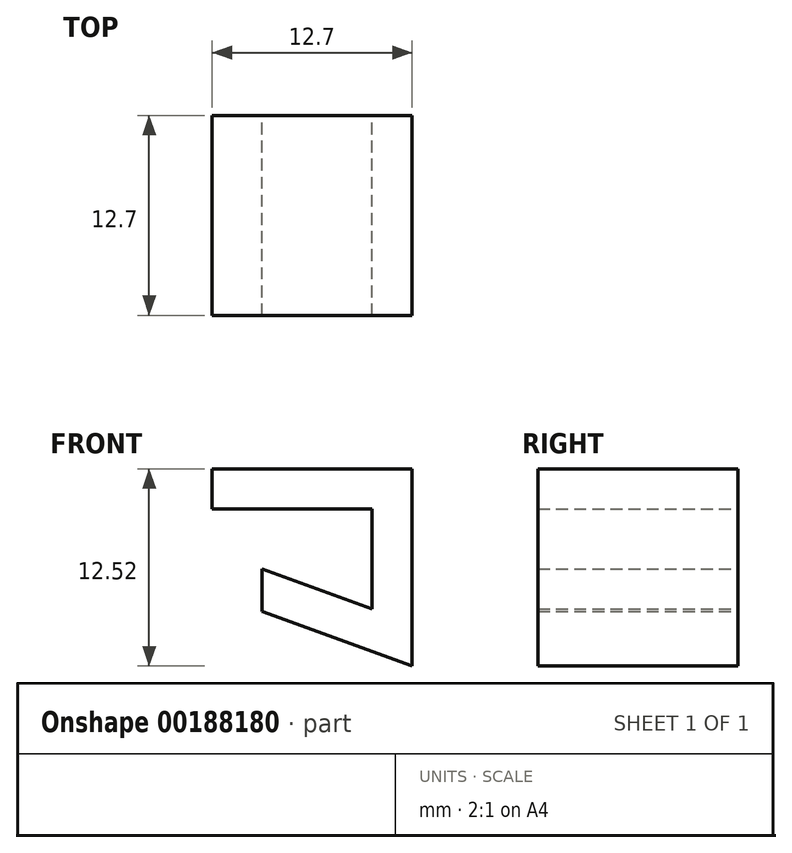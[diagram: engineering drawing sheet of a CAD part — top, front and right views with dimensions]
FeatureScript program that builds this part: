
annotation { "Feature Type Name" : "Feature", "Feature Type Description" : "" }
export const myFeature = defineFeature(function(context is Context, id is Id, definition is map)
    precondition{}
    {
        {
            var Q0;
            Q0=qCreatedBy(makeId("Front.planeOp"),FACE);
            var sketch = newSketch(context, id + "F0", { "sketchPlane" : qUnion([Q0])});
            skLineSegment(sketch, "E0", {"start": v(3.17, -6.35) * mm, "end": v(10.16, -8.89) * mm});
            skLineSegment(sketch, "E1", {"start": v(10.16, -8.89) * mm, "end": v(10.16, -2.54) * mm});
            skLineSegment(sketch, "E2", {"start": v(10.16, -2.54) * mm, "end": v(0, -2.54) * mm});
            skLineSegment(sketch, "E3.1", {"start": v(3.17, -9.05) * mm, "end": v(12.7, -12.52) * mm});
            skLineSegment(sketch, "E3.2", {"start": v(12.7, -12.52) * mm, "end": v(12.7, 0) * mm});
            skLineSegment(sketch, "E3.3", {"start": v(12.7, 0) * mm, "end": v(0, 0) * mm});
            skLineSegment(sketch, "E4", {"start": v(3.18, -6.35) * mm, "end": v(3.18, -9.05) * mm});
            skLineSegment(sketch, "E5", {"start": v(0, 0) * mm, "end": v(0, -2.54) * mm});
            skSolve(sketch);
        }
        {
            var Q0;
            Q0=makeQuery(id+"F0.imprint","IMPRINT",FACE,{"disambiguationData":[TD([[makeQuery(id+"F0.imprint","IMPRINT",EDGE,{"derivedFrom":sQuery(id+"F0.wireOp",EDGE,"E0")}),-1.0]])]});
            extrude(context, id + "F1", {"entities" : qUnion([Q0]), "depth" : 12.7 * mm});
        }
    });
